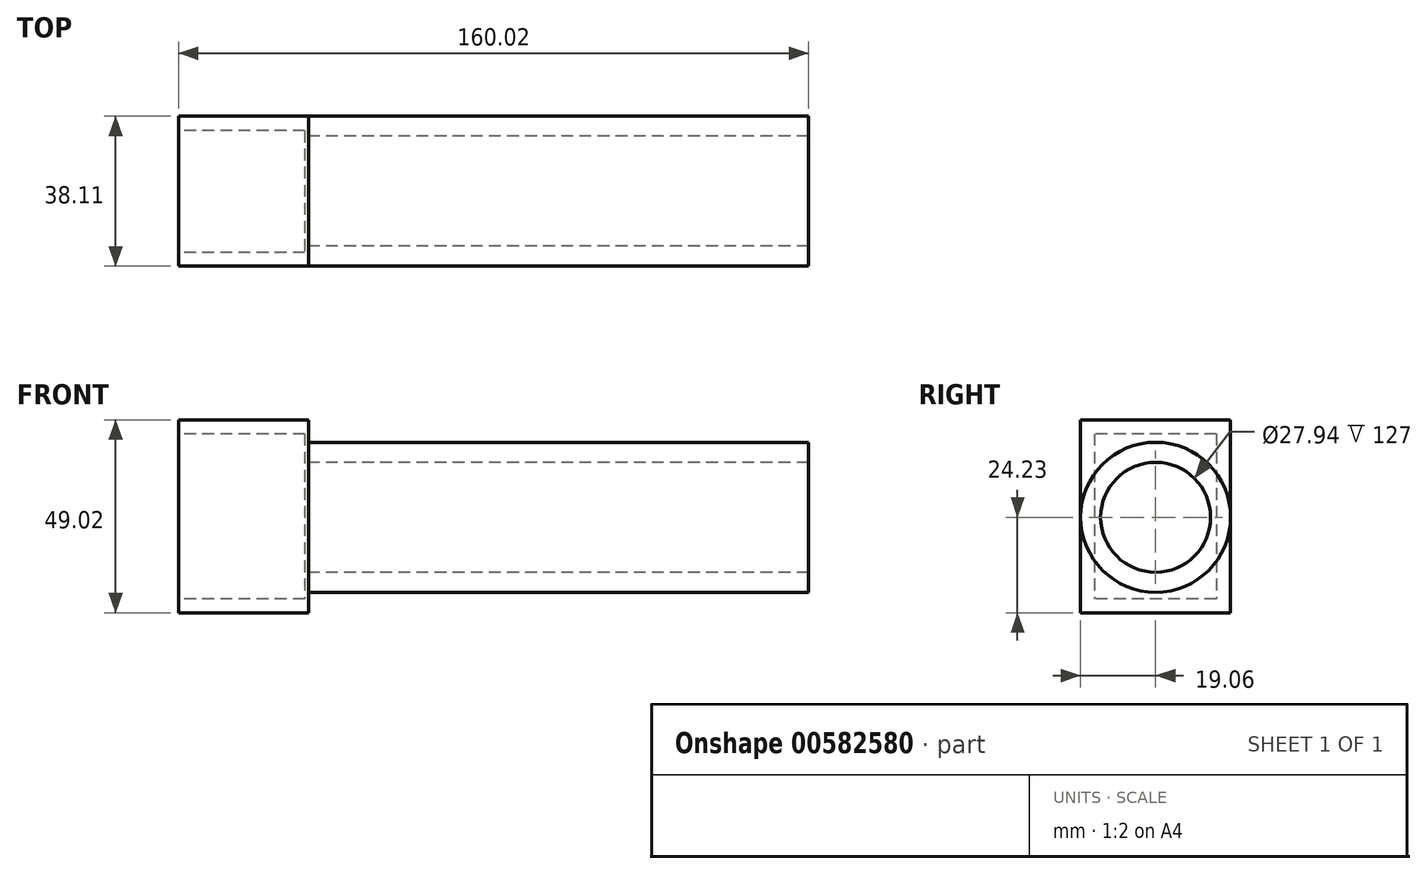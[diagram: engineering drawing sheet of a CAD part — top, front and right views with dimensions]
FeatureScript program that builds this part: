
annotation { "Feature Type Name" : "Feature", "Feature Type Description" : "" }
export const myFeature = defineFeature(function(context is Context, id is Id, definition is map)
    precondition{}
    {
        {
            var Q0;
            Q0=qCreatedBy(makeId("Right.planeOp"),FACE);
            var sketch = newSketch(context, id + "F0", { "sketchPlane" : qUnion([Q0])});
            skCircle(sketch, "E0", {"center": v(0, 0) * mm, "radius": 19.05 * mm});
            skCircle(sketch, "E1.0", {"center": v(0, 0) * mm, "radius": 13.97 * mm});
            skSolve(sketch);
        }
        {
            var Q0;
            Q0=makeQuery(id+"F0.imprint","IMPRINT",FACE,{"disambiguationData":[TD([[makeQuery(id+"F0.imprint","IMPRINT",EDGE,{"derivedFrom":sQuery(id+"F0.wireOp",EDGE,"E0")}),-1.0]])]});
            var Q1;
            Q1=makeQuery(id+"F0.imprint","IMPRINT",FACE,{"disambiguationData":[TD([[makeQuery(id+"F0.imprint","IMPRINT",EDGE,{"derivedFrom":sQuery(id+"F0.wireOp",EDGE,"E0")}),1.0]])]});
            var Q2;
            Q2=sQuery(id+"F0.wireOp",EDGE,"E1.0");
            var Q3;
            Q3=sQuery(id+"F0.wireOp",EDGE,"E0");
            extrude(context, id + "F1", {"entities" : qUnion([Q0, Q1]), "surfaceEntities" : qUnion([Q2, Q3]), "depth" : 127 * mm, "offsetDistance" : 25.4 * mm});
        }
        {
            var Q0;
            Q0=qCreatedBy(makeId("Right.planeOp"),FACE);
            var sketch = newSketch(context, id + "F2", { "sketchPlane" : qUnion([Q0])});
            skLineSegment(sketch, "E2.0", {"start": v(-19.06, -24.23) * mm, "end": v(19.04, -24.23) * mm});
            skLineSegment(sketch, "E2.1", {"start": v(19.04, 24.79) * mm, "end": v(19.04, -24.23) * mm});
            skLineSegment(sketch, "E2.2", {"start": v(-19.06, 24.79) * mm, "end": v(19.04, 24.79) * mm});
            skLineSegment(sketch, "E3", {"start": v(-19.06, 24.79) * mm, "end": v(-19.06, -24.23) * mm});
            skLineSegment(sketch, "E4.0", {"start": v(-15.5, 21.23) * mm, "end": v(15.49, 21.23) * mm});
            skLineSegment(sketch, "E4.1", {"start": v(-15.5, 21.23) * mm, "end": v(-15.5, -20.68) * mm});
            skLineSegment(sketch, "E4.2", {"start": v(-15.5, -20.68) * mm, "end": v(15.49, -20.68) * mm});
            skLineSegment(sketch, "E4.3", {"start": v(15.49, 21.23) * mm, "end": v(15.49, -20.68) * mm});
            skSolve(sketch);
        }
        {
            var Q0;
            Q0 = qSketchRegion(id + "F2", true);
            var Q1;
            Q1=makeQuery(id+"F2.imprint","IMPRINT",FACE,{"disambiguationData":[TD([[makeQuery(id+"F2.imprint","IMPRINT",EDGE,{"derivedFrom":sQuery(id+"F2.wireOp",EDGE,"E4.0")}),-1.0]])]});
            var Q2;
            Q2=sQuery(id+"F2.wireOp",EDGE,"E4.1");
            var Q3;
            Q3=sQuery(id+"F2.wireOp",EDGE,"E4.2");
            var Q4;
            Q4=sQuery(id+"F2.wireOp",EDGE,"E4.3");
            var Q5;
            Q5=sQuery(id+"F2.wireOp",EDGE,"E4.0");
            extrude(context, id + "F3", {"entities" : qUnion([Q0, Q1]), "surfaceEntities" : qUnion([Q2, Q3, Q4, Q5]), "oppositeDirection" : true, "depth" : 33.02 * mm, "offsetDistance" : 25.4 * mm});
        }
        {
            var Q0;
            Q0=qCreatedBy(makeId("Top.planeOp"),FACE);
            var sketch = newSketch(context, id + "F4", { "sketchPlane" : qUnion([Q0])});
            skLineSegment(sketch, "E5", {"start": v(126.57, 19.5) * mm, "end": v(126.57, 49.37) * mm});
            skFitSpline(sketch, "E6", {"points": [v(126.57, 49.37) * mm, v(99.74, 44.23) * mm, v(61.08, 18.98) * mm, v(61.08, 18.82) * mm], "startDerivative": vector(-54.07, 5.5) * mm, "endDerivative": vector(2.3, -3.28) * mm});
            skFitSpline(sketch, "E7.MirrorCS", {"points": [v(126.57, -49.37) * mm, v(99.74, -44.23) * mm, v(61.08, -18.98) * mm, v(61.08, -18.82) * mm], "startDerivative": vector(-54.07, -5.5) * mm, "endDerivative": vector(2.3, 3.28) * mm});
            skLineSegment(sketch, "E8.MirrorCS", {"start": v(126.57, -19.5) * mm, "end": v(126.57, -49.37) * mm});
            skSolve(sketch);
        }
        {
            var Q0;
            Q0=sQuery(id+"F4.wireOp",EDGE,"E8.MirrorCS");
            var Q1;
            Q1=sQuery(id+"F4.wireOp",EDGE,"E7.MirrorCS");
            var Q2;
            Q2=sQuery(id+"F4.wireOp",EDGE,"E5");
            var Q3;
            Q3=sQuery(id+"F4.wireOp",EDGE,"E6");
            extrude(context, id + "F5", {"bodyType" : ToolBodyType.SURFACE, "operationType" : NewBodyOperationType.REMOVE, "surfaceEntities" : qUnion([Q0, Q1, Q2, Q3]), "endBound" : BoundingType.SYMMETRIC, "depth" : 6.35 * mm, "offsetDistance" : 25.4 * mm});
        }
        {
            var Q0;
            Q0=qCreatedBy(makeId("Front.planeOp"),FACE);
            var sketch = newSketch(context, id + "F6", { "sketchPlane" : qUnion([Q0])});
            skLineSegment(sketch, "E9", {"start": v(126.96, -18.78) * mm, "end": v(126.96, -49.3) * mm});
            skFitSpline(sketch, "E10.MirrorCS", {"points": [v(126.7, -49.17) * mm, v(99.87, -44.03) * mm, v(61.2, -18.78) * mm, v(61.2, -18.62) * mm], "startDerivative": vector(-54.07, -5.5) * mm, "endDerivative": vector(2.3, 3.28) * mm});
            skLineSegment(sketch, "E11", {"start": v(188.2, 0) * mm, "end": v(-52.5, 0) * mm, "construction": true});
            skLineSegment(sketch, "E12.MirrorCS", {"start": v(126.96, 18.78) * mm, "end": v(126.96, 49.3) * mm});
            skFitSpline(sketch, "E13.MirrorCS", {"points": [v(126.7, 49.17) * mm, v(99.87, 44.03) * mm, v(61.2, 18.78) * mm, v(61.2, 18.62) * mm], "startDerivative": vector(-54.07, 5.5) * mm, "endDerivative": vector(2.3, -3.28) * mm});
            skSolve(sketch);
        }
        {
            var Q0;
            Q0 = qSketchRegion(id + "F6", true);
            var Q1;
            Q1=sQuery(id+"F6.wireOp",EDGE,"E10.MirrorCS");
            var Q2;
            Q2=sQuery(id+"F6.wireOp",EDGE,"E9");
            var Q3;
            Q3=sQuery(id+"F6.wireOp",EDGE,"E12.MirrorCS");
            var Q4;
            Q4=sQuery(id+"F6.wireOp",EDGE,"E13.MirrorCS");
            extrude(context, id + "F7", {"entities" : qUnion([Q0]), "bodyType" : ToolBodyType.SURFACE, "surfaceEntities" : qUnion([Q1, Q2, Q3, Q4]), "endBound" : BoundingType.SYMMETRIC, "depth" : 6.35 * mm, "offsetDistance" : 25.4 * mm});
        }
        {
            var Q0;
            Q0=makeQuery(id+"F3.opExtrude","CAP_FACE",FACE,{"disambiguationData":[OSD([sQuery(id+"F2.wireOp",EDGE,"E2.0"),sQuery(id+"F2.wireOp",EDGE,"E2.1"),sQuery(id+"F2.wireOp",EDGE,"E2.2"),sQuery(id+"F2.wireOp",EDGE,"E3")])],"isStart":false});
            var sketch = newSketch(context, id + "F8", { "sketchPlane" : qUnion([Q0])});
            skLineSegment(sketch, "E14.0", {"start": v(-15.41, 21.23) * mm, "end": v(15.57, 21.23) * mm});
            skLineSegment(sketch, "E14.1", {"start": v(-15.41, 21.23) * mm, "end": v(-15.41, -20.68) * mm});
            skLineSegment(sketch, "E14.2", {"start": v(-15.41, -20.68) * mm, "end": v(15.57, -20.68) * mm});
            skLineSegment(sketch, "E14.3", {"start": v(15.57, 21.23) * mm, "end": v(15.57, -20.68) * mm});
            skSolve(sketch);
        }
        {
            var Q0;
            Q0=makeQuery(id+"F8.imprint","IMPRINT",FACE,{"disambiguationData":[TD([[makeQuery(id+"F8.imprint","IMPRINT",EDGE,{"derivedFrom":sQuery(id+"F8.wireOp",EDGE,"E14.0")}),-1.0]])]});
            extrude(context, id + "F9", {"entities" : qUnion([Q0]), "operationType" : NewBodyOperationType.REMOVE, "oppositeDirection" : true, "depth" : 32 * mm, "offsetDistance" : 25.4 * mm});
        }
    });
